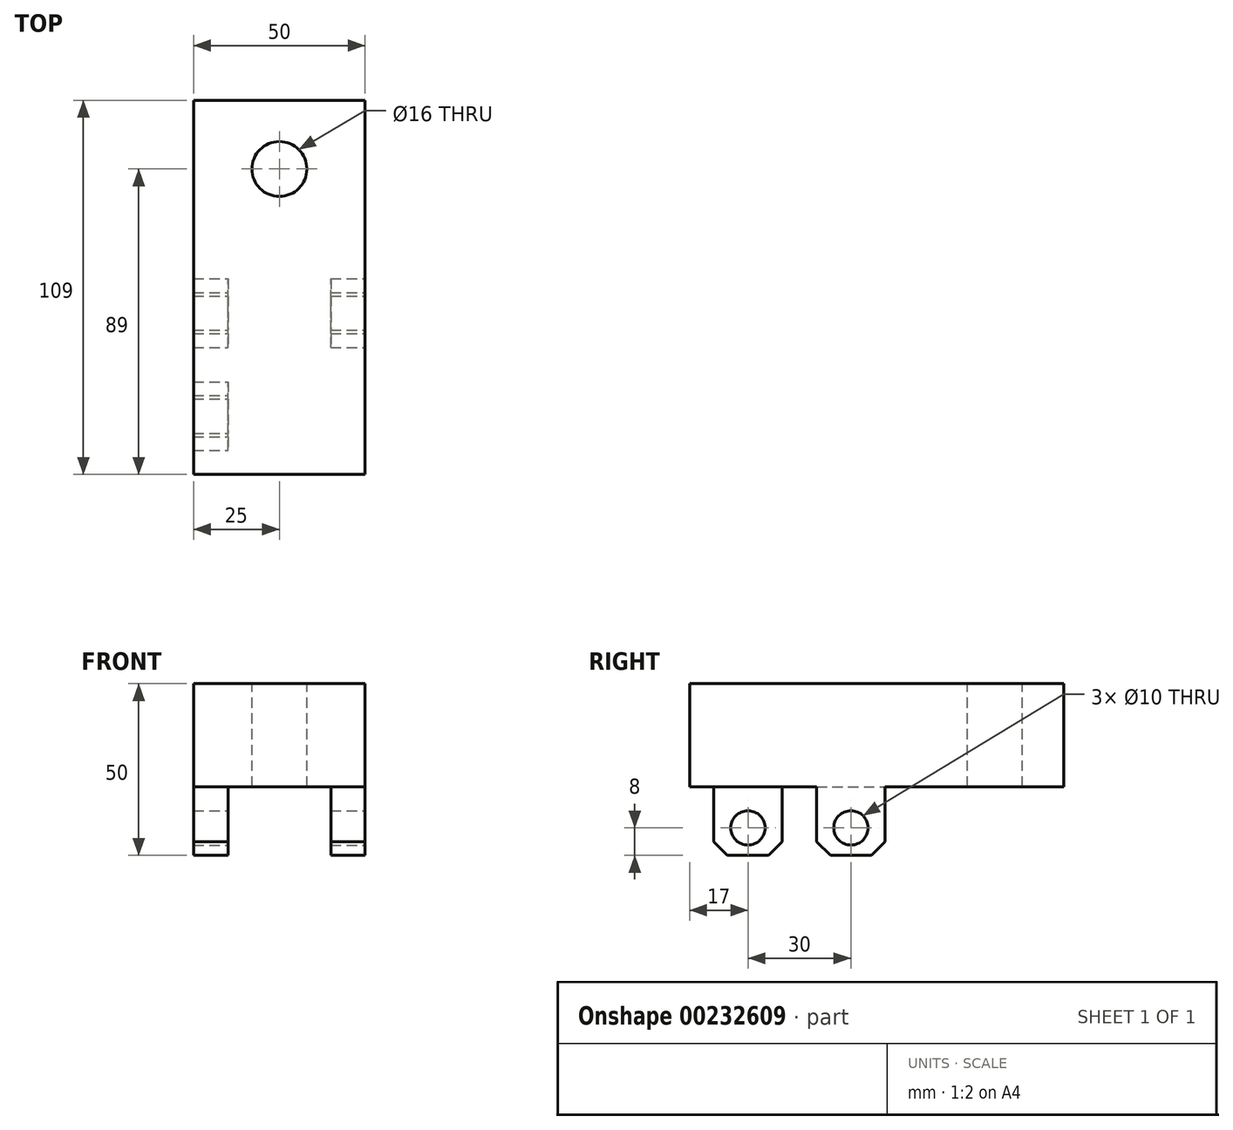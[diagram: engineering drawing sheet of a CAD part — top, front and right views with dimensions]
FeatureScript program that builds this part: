
annotation { "Feature Type Name" : "Feature", "Feature Type Description" : "" }
export const myFeature = defineFeature(function(context is Context, id is Id, definition is map)
    precondition{}
    {
        {
            var Q0;
            Q0=qCreatedBy(makeId("Front.planeOp"),FACE);
            var sketch = newSketch(context, id + "F0", { "sketchPlane" : qUnion([Q0])});
            skLineSegment(sketch, "E0.bottom", {"start": v(0, 0) * mm, "end": v(50, 0) * mm});
            skLineSegment(sketch, "E0.top", {"start": v(0, 30) * mm, "end": v(50, 30) * mm});
            skLineSegment(sketch, "E0.left", {"start": v(0, 0) * mm, "end": v(0, 30) * mm});
            skLineSegment(sketch, "E0.right", {"start": v(50, 0) * mm, "end": v(50, 30) * mm});
            skSolve(sketch);
        }
        {
            var Q0;
            Q0 = qSketchRegion(id + "F0", true);
            extrude(context, id + "F1", {"entities" : qUnion([Q0]), "depth" : 109 * mm});
        }
        {
            var Q0;
            Q0=makeQuery(id+"F1.opExtrude","SWEPT_FACE",FACE,{"disambiguationData":[OSD([sQuery(id+"F0.wireOp",EDGE,"E0.top")])]});
            var sketch = newSketch(context, id + "F2", { "sketchPlane" : qUnion([Q0])});
            skCircle(sketch, "E1", {"center": v(25, -20) * mm, "radius": 8 * mm});
            skSolve(sketch);
        }
        {
            var Q0;
            Q0 = qSketchRegion(id + "F2", true);
            extrude(context, id + "F3", {"entities" : qUnion([Q0]), "operationType" : NewBodyOperationType.REMOVE, "endBound" : BoundingType.THROUGH_ALL, "oppositeDirection" : true, "depth" : 25 * mm});
        }
        {
            var Q0;
            Q0=makeQuery(id+"F1.opExtrude","SWEPT_FACE",FACE,{"disambiguationData":[OSD([sQuery(id+"F0.wireOp",EDGE,"E0.right")])]});
            var sketch = newSketch(context, id + "F4", { "sketchPlane" : qUnion([Q0])});
            skLineSegment(sketch, "E2.MirrorCS", {"start": v(-72, 0) * mm, "end": v(-72, -16) * mm});
            skLineSegment(sketch, "E3.MirrorCS", {"start": v(-52, -16) * mm, "end": v(-52, 0) * mm});
            skLineSegment(sketch, "E4.MirrorCS", {"start": v(-56, -20) * mm, "end": v(-52, -16) * mm});
            skLineSegment(sketch, "E5.MirrorCS", {"start": v(-68, -20) * mm, "end": v(-56, -20) * mm});
            skLineSegment(sketch, "E6.MirrorCS", {"start": v(-72, -16) * mm, "end": v(-68, -20) * mm});
            skCircle(sketch, "E7.MirrorC", {"center": v(-62, -12) * mm, "radius": 5 * mm});
            skLineSegment(sketch, "E8.MirrorCS", {"start": v(-52, 0) * mm, "end": v(-72, 0) * mm});
            skLineSegment(sketch, "E9.MirrorCS", {"start": v(-102, 0) * mm, "end": v(-102, -16) * mm});
            skLineSegment(sketch, "E10.MirrorCS", {"start": v(-82, -16) * mm, "end": v(-82, 0) * mm});
            skLineSegment(sketch, "E11.MirrorCS", {"start": v(-86, -20) * mm, "end": v(-82, -16) * mm});
            skLineSegment(sketch, "E12.MirrorCS", {"start": v(-98, -20) * mm, "end": v(-86, -20) * mm});
            skLineSegment(sketch, "E13.MirrorCS", {"start": v(-102, -16) * mm, "end": v(-98, -20) * mm});
            skCircle(sketch, "E14.MirrorC", {"center": v(-92, -12) * mm, "radius": 5 * mm});
            skLineSegment(sketch, "E15.MirrorCS", {"start": v(-82, 0) * mm, "end": v(-102, 0) * mm});
            skSolve(sketch);
        }
        {
            var Q0;
            Q0 = qSketchRegion(id + "F4", true);
            extrude(context, id + "F5", {"entities" : qUnion([Q0]), "operationType" : NewBodyOperationType.ADD, "oppositeDirection" : true, "depth" : 50 * mm});
        }
        {
            var Q0;
            Q0=makeQuery(id+"F1.opExtrude","CAP_FACE",FACE,{"disambiguationData":[OSD([sQuery(id+"F0.wireOp",EDGE,"E0.bottom"),sQuery(id+"F0.wireOp",EDGE,"E0.top"),sQuery(id+"F0.wireOp",EDGE,"E0.left"),sQuery(id+"F0.wireOp",EDGE,"E0.right")])],"isStart":true});
            var sketch = newSketch(context, id + "F6", { "sketchPlane" : qUnion([Q0])});
            skLineSegment(sketch, "E16.bottom", {"start": v(-40, 0) * mm, "end": v(-10, 0) * mm});
            skLineSegment(sketch, "E16.top", {"start": v(-40, -20) * mm, "end": v(-10, -20) * mm});
            skLineSegment(sketch, "E16.left", {"start": v(-40, 0) * mm, "end": v(-40, -20) * mm});
            skLineSegment(sketch, "E16.right", {"start": v(-10, 0) * mm, "end": v(-10, -20) * mm});
            skSolve(sketch);
        }
        {
            var Q0;
            Q0 = qSketchRegion(id + "F6", true);
            extrude(context, id + "F7", {"entities" : qUnion([Q0]), "operationType" : NewBodyOperationType.REMOVE, "endBound" : BoundingType.THROUGH_ALL, "oppositeDirection" : true, "depth" : 25 * mm});
        }
        {
            var Q0;
            Q0=makeQuery(id+"F5.boolean.opBoolean","MERGE",FACE,{"derivedFrom":[makeQuery(id+"F1.opExtrude","SWEPT_FACE",FACE,{"disambiguationData":[OSD([sQuery(id+"F0.wireOp",EDGE,"E0.right")])]}),makeQuery(id+"F5.opExtrude","CAP_FACE",FACE,{"disambiguationData":[OSD([sQuery(id+"F4.wireOp",EDGE,"E2.MirrorCS"),sQuery(id+"F4.wireOp",EDGE,"E3.MirrorCS"),sQuery(id+"F4.wireOp",EDGE,"E4.MirrorCS"),sQuery(id+"F4.wireOp",EDGE,"E5.MirrorCS"),sQuery(id+"F4.wireOp",EDGE,"E6.MirrorCS"),sQuery(id+"F4.wireOp",EDGE,"E7.MirrorC"),sQuery(id+"F4.wireOp",EDGE,"E8.MirrorCS")])],"isStart":true}),makeQuery(id+"F5.opExtrude","CAP_FACE",FACE,{"disambiguationData":[OSD([sQuery(id+"F4.wireOp",EDGE,"E9.MirrorCS"),sQuery(id+"F4.wireOp",EDGE,"E10.MirrorCS"),sQuery(id+"F4.wireOp",EDGE,"E11.MirrorCS"),sQuery(id+"F4.wireOp",EDGE,"E12.MirrorCS"),sQuery(id+"F4.wireOp",EDGE,"E13.MirrorCS"),sQuery(id+"F4.wireOp",EDGE,"E14.MirrorC"),sQuery(id+"F4.wireOp",EDGE,"E15.MirrorCS")])],"isStart":true})]});
            var sketch = newSketch(context, id + "F8", { "sketchPlane" : qUnion([Q0])});
            skLineSegment(sketch, "E17.bottom", {"start": v(-102, 0) * mm, "end": v(-82, 0) * mm});
            skLineSegment(sketch, "E17.top", {"start": v(-102, -20) * mm, "end": v(-82, -20) * mm});
            skLineSegment(sketch, "E17.left", {"start": v(-82, 0) * mm, "end": v(-82, -20) * mm});
            skLineSegment(sketch, "E17.right", {"start": v(-102, 0) * mm, "end": v(-102, -20) * mm});
            skSolve(sketch);
        }
        {
            var Q0;
            Q0 = qSketchRegion(id + "F8", true);
            extrude(context, id + "F9", {"entities" : qUnion([Q0]), "operationType" : NewBodyOperationType.REMOVE, "oppositeDirection" : true, "depth" : 25 * mm});
        }
    });
